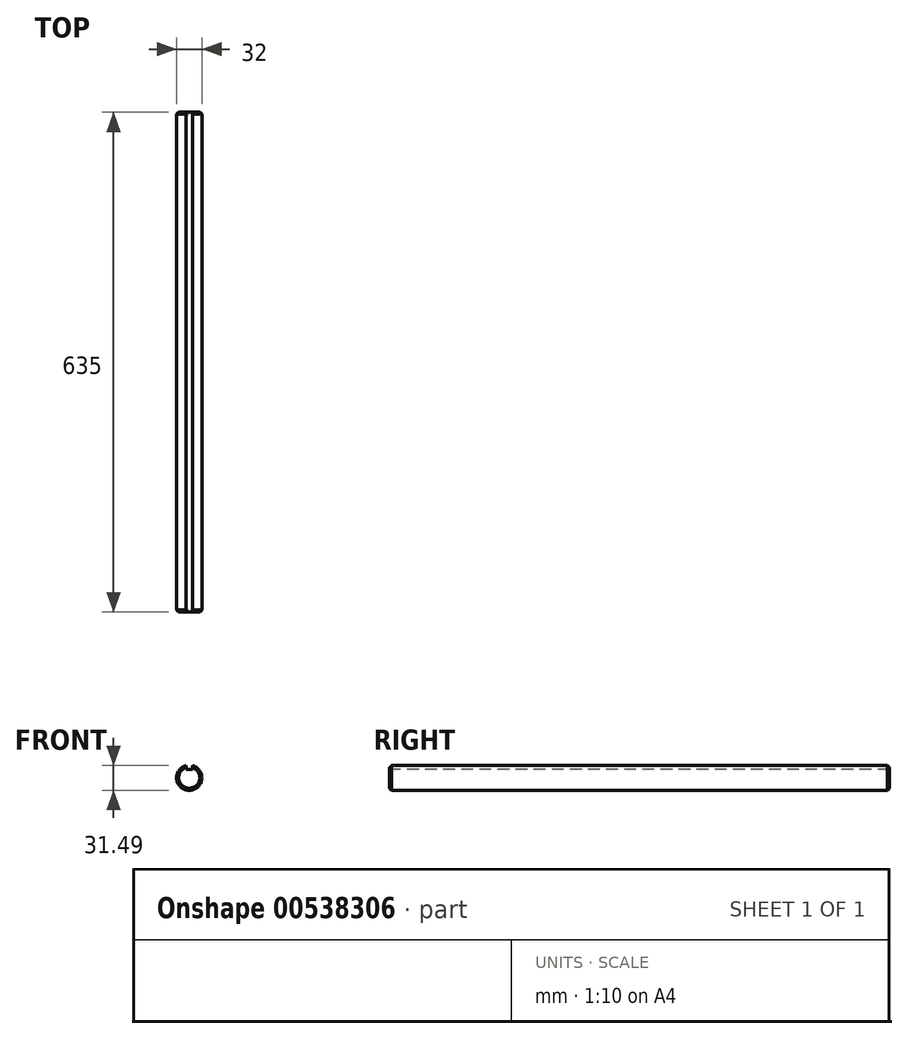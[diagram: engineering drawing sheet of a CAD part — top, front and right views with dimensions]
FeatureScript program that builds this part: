
annotation { "Feature Type Name" : "Feature", "Feature Type Description" : "" }
export const myFeature = defineFeature(function(context is Context, id is Id, definition is map)
    precondition{}
    {
        {
            var Q0;
            Q0=qCreatedBy(makeId("Front.planeOp"),FACE);
            var sketch = newSketch(context, id + "F0", { "sketchPlane" : qUnion([Q0])});
            skCircle(sketch, "E0", {"center": v(0, 0) * mm, "radius": 16 * mm});
            skSolve(sketch);
        }
        {
            var Q0;
            Q0 = qSketchRegion(id + "F0", true);
            extrude(context, id + "F1", {"entities" : qUnion([Q0]), "depth" : 635 * mm, "offsetDistance" : 25.4 * mm});
        }
        {
            var Q0;
            Q0=makeQuery(id+"F1.opExtrude","CAP_EDGE",EDGE,{"disambiguationData":[OSD([sQuery(id+"F0.wireOp",EDGE,"E0")])],"isStart":true});
            var Q1;
            Q1=makeQuery(id+"F1.opExtrude","CAP_EDGE",EDGE,{"disambiguationData":[OSD([sQuery(id+"F0.wireOp",EDGE,"E0")])],"isStart":false});
            chamfer(context, id + "F2", {"entities" : qUnion([Q0, Q1]), "width" : 2.54 * mm, "tangentPropagation" : true});
        }
        {
            var Q0;
            Q0=makeQuery(id+"F1.opExtrude","CAP_FACE",FACE,{"disambiguationData":[OSD([sQuery(id+"F0.wireOp",EDGE,"E0")])],"isStart":false});
            var sketch = newSketch(context, id + "F3", { "sketchPlane" : qUnion([Q0])});
            skLineSegment(sketch, "E1.bottom", {"start": v(4, 10.46) * mm, "end": v(-4, 10.46) * mm});
            skLineSegment(sketch, "E1.top", {"start": v(4, 16.46) * mm, "end": v(-4, 16.46) * mm});
            skLineSegment(sketch, "E1.left", {"start": v(4, 10.46) * mm, "end": v(4, 16.46) * mm});
            skLineSegment(sketch, "E1.right", {"start": v(-4, 10.46) * mm, "end": v(-4, 16.46) * mm});
            skPoint(sketch, "E1.middle", {"position": v(0, 13.46) * mm});
            skSolve(sketch);
        }
        {
            var Q0;
            Q0 = qSketchRegion(id + "F3", true);
            extrude(context, id + "F4", {"entities" : qUnion([Q0]), "operationType" : NewBodyOperationType.REMOVE, "endBound" : BoundingType.THROUGH_ALL, "oppositeDirection" : true, "depth" : 25.4 * mm, "offsetDistance" : 25.4 * mm});
        }
    });
